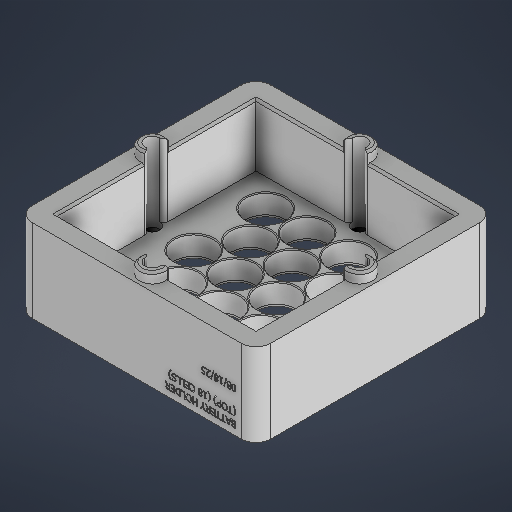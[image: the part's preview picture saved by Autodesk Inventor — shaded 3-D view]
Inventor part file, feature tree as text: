
AUTODESK INVENTOR PART (.ipt)
format: ipt  version: 2025 (Build 290162000, 162)  size: 1,048,576 bytes
history: native  units: in
note: dims shown in document units (in); Inventor stores cm internally (conversion verified against a paired STEP export)
features: sketch x8, extrude x4, hole x2, fillet x2, chamfer x2
ambient origin geometry x8: Origin, YZ Plane, XZ Plane, XY Plane, X Axis, Y Axis, Z Axis, Center Point
bodies: Solid1 (feature_tree)
feature tree (18):
  extrude  "Extrusion1"  Depth=4.5276in
  sketch  "Sketch4"  dims[d2=0.3937in d3=0.0in d48=3.7795in]
  extrude  "Extrusion3"  Depth=3.7795in
  hole  "Hole4"  [1 undecoded]
  hole  "Hole5"  [1 undecoded]
  extrude  "Extrusion4"  Depth=1.5748in
  fillet  "Fillet1"  Radius=0.748in
  fillet  "Fillet2"  Radius=0.3937in
  chamfer  "Chamfer1"  Distance=1.1811in
  chamfer  "Chamfer2"  Distance=3.937in
  extrude  "Extrusion5"  Depth=3.937in
  sketch  "Sketch1"  dims[d0=4.5276in d1=4.5276in]
  sketch  "Sketch Rectangular Pattern11"  dims[d147=0.6819in]
  sketch  "Sketch Rectangular Pattern12"  dims[d148=1.1811in d150=0.7874in d151=0.7874in d153=1.3638in d174=1.1811in d175=0.0in]
  sketch  "Sketch6"  dims[d49=3.7795in d124=1.3638in]
  sketch  "Sketch Rectangular Pattern14"  dims[d176=0.7323in d177=0.2362in d178=0.748in d179=0.0787in d180=0.0172in d181=0.315in d182=0.8108in d183=3.937in d184=3.937in d185=0.2362in d186=1.1811in d188=1.9685in d189=1.1811in d191=1.9685in d194=0.2805in d195=0.2362in d196=0.5118in d197=0.2756in d198=0.0172in d199=0.315in d200=0.8108in d201=0.4724in d202=0.4724in d203=0.4724in d204=0.4724in d205=0.1969in d206=0.0in d207=0.2805in d208=0.0787in d209=0.0157in d210=0.0787in d211=45.0deg d212=0.0394in d213=0.0787in d214=45.0deg d215=0.0787in d216=0.0in]
  sketch  "Sketch7"  dims[d132=2.3622in d133=2.7276in]
  sketch  "Sketch8"  dims[d134=0.748in d135=1.5748in d137=0.7874in d138=1.1811in d140=1.3638in d143=0.748in d146=0.3937in]
note: 2 required parameter values undecoded (feature->parameter linkage not recoverable at this tier; creation-order binding heuristic only, values carry confidence <= 0.55)
